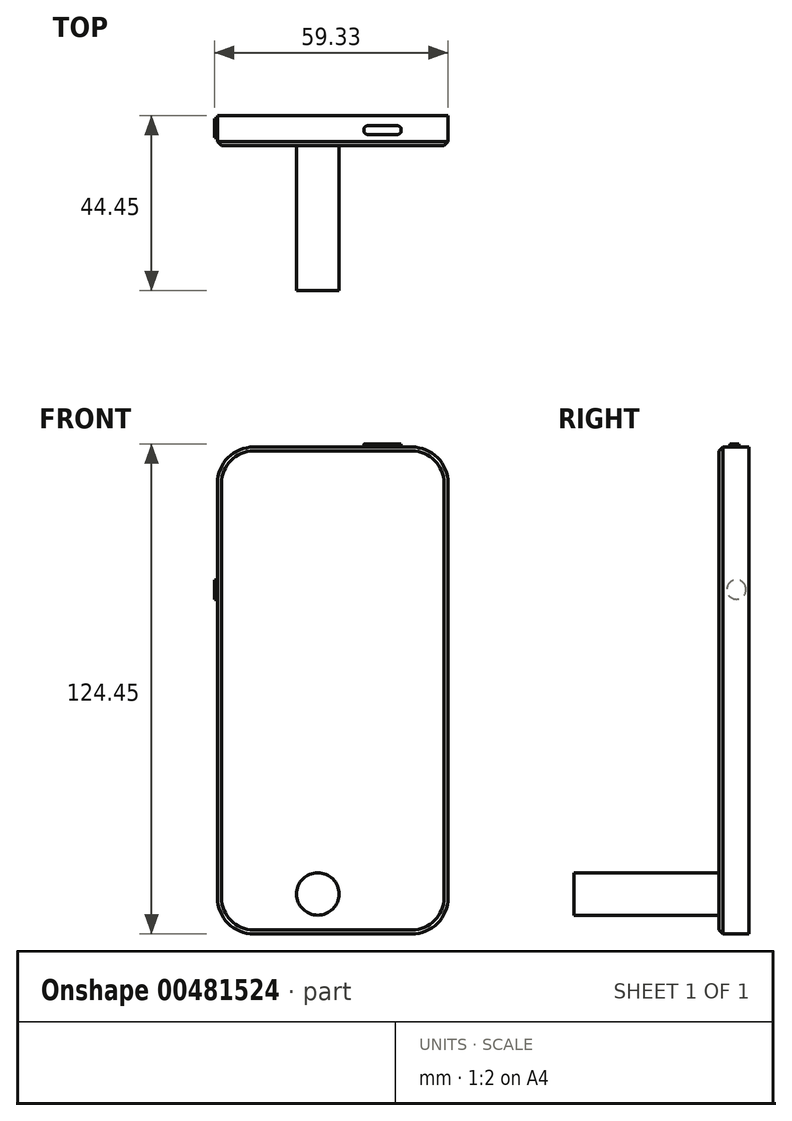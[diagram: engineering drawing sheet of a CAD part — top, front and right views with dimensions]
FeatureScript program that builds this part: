
annotation { "Feature Type Name" : "Feature", "Feature Type Description" : "" }
export const myFeature = defineFeature(function(context is Context, id is Id, definition is map)
    precondition{}
    {
        {
            var Q0;
            Q0=qCreatedBy(makeId("Front.planeOp"),FACE);
            var sketch = newSketch(context, id + "F0", { "sketchPlane" : qUnion([Q0])});
            skLineSegment(sketch, "E0.bottom", {"start": v(-62.59, 53.88) * mm, "end": v(-4.02, 53.88) * mm});
            skLineSegment(sketch, "E0.top", {"start": v(-62.59, -69.81) * mm, "end": v(-4.02, -69.81) * mm});
            skLineSegment(sketch, "E0.left", {"start": v(-62.59, 53.88) * mm, "end": v(-62.59, -69.81) * mm});
            skLineSegment(sketch, "E0.right", {"start": v(-4.02, 53.88) * mm, "end": v(-4.02, -69.81) * mm});
            skSolve(sketch);
        }
        {
            var Q0;
            Q0 = qSketchRegion(id + "F0", true);
            extrude(context, id + "F1", {"entities" : qUnion([Q0]), "depth" : 7.62 * mm});
        }
        {
            var Q0;
            Q0=makeQuery(id+"F1.opExtrude","SWEPT_EDGE",EDGE,{"disambiguationData":[OSD([sQuery(id+"F0.wireOp",EDGE,"E0.top"),sQuery(id+"F0.wireOp",EDGE,"E0.left")])]});
            var Q1;
            Q1=makeQuery(id+"F1.opExtrude","SWEPT_EDGE",EDGE,{"disambiguationData":[OSD([sQuery(id+"F0.wireOp",EDGE,"E0.top"),sQuery(id+"F0.wireOp",EDGE,"E0.right")])]});
            var Q2;
            Q2=makeQuery(id+"F1.opExtrude","SWEPT_EDGE",EDGE,{"disambiguationData":[OSD([sQuery(id+"F0.wireOp",EDGE,"E0.bottom"),sQuery(id+"F0.wireOp",EDGE,"E0.right")])]});
            var Q3;
            Q3=makeQuery(id+"F1.opExtrude","SWEPT_EDGE",EDGE,{"disambiguationData":[OSD([sQuery(id+"F0.wireOp",EDGE,"E0.bottom"),sQuery(id+"F0.wireOp",EDGE,"E0.left")])]});
            fillet(context, id + "F2", {"entities" : qUnion([Q0, Q1, Q2, Q3]), "radius" : 9.16 * mm, "tangentPropagation" : true, "allowEdgeOverflow" : false});
        }
        {
            var Q0;
            Q0=makeQuery(id+"F1.opExtrude","CAP_EDGE",EDGE,{"disambiguationData":[OSD([sQuery(id+"F0.wireOp",EDGE,"E0.bottom")])],"isStart":false});
            chamfer(context, id + "F3", {"entities" : qUnion([Q0]), "width" : 1.02 * mm, "tangentPropagation" : true});
        }
        {
            var Q0;
            Q0=qCreatedBy(makeId("Top.planeOp"),FACE);
            var sketch = newSketch(context, id + "F4", { "sketchPlane" : qUnion([Q0])});
            skLineSegment(sketch, "E1.bottom", {"start": v(-59.32, -32.86) * mm, "end": v(-49.82, -32.86) * mm});
            skLineSegment(sketch, "E1.top", {"start": v(-59.32, -35.06) * mm, "end": v(-49.82, -35.06) * mm});
            skLineSegment(sketch, "E1.left", {"start": v(-59.32, -32.86) * mm, "end": v(-59.32, -35.06) * mm});
            skLineSegment(sketch, "E1.right", {"start": v(-49.82, -32.86) * mm, "end": v(-49.82, -35.06) * mm});
            skSolve(sketch);
        }
        {
            var Q0;
            Q0=makeQuery(id+"F4.imprint","IMPRINT",FACE,{"disambiguationData":[TD([[makeQuery(id+"F4.imprint","IMPRINT",EDGE,{"derivedFrom":sQuery(id+"F4.wireOp",EDGE,"E1.bottom")}),-1.0]])]});
            extrude(context, id + "F5", {"entities" : qUnion([Q0]), "depth" : 0.76 * mm});
        }
        {
            var Q0;
            Q0=makeQuery(id+"F5.opExtrude","SWEPT_BODY",BODY,{"disambiguationData":[OSD([sQuery(id+"F4.wireOp",EDGE,"E1.bottom"),sQuery(id+"F4.wireOp",EDGE,"E1.top"),sQuery(id+"F4.wireOp",EDGE,"E1.left"),sQuery(id+"F4.wireOp",EDGE,"E1.right")])]});
            transform(context, id + "F6", {"entities" : qUnion([Q0]), "transformType" : TransformType.TRANSLATION_3D, "dx" : 27.3 * mm, "dy" : 23.14 * mm, "dz" : 53.87 * mm, "makeCopy" : false});
        }
        {
            var Q0;
            Q0=makeQuery(id+"F5.opExtrude","SWEPT_BODY",BODY,{"disambiguationData":[OSD([sQuery(id+"F4.wireOp",EDGE,"E1.bottom"),sQuery(id+"F4.wireOp",EDGE,"E1.top"),sQuery(id+"F4.wireOp",EDGE,"E1.left"),sQuery(id+"F4.wireOp",EDGE,"E1.right")])]});
            transform(context, id + "F7", {"entities" : qUnion([Q0]), "transformType" : TransformType.TRANSLATION_3D, "dx" : 6.6 * mm, "dy" : 4.06 * mm, "dz" : 0 * mm, "makeCopy" : false});
        }
        {
            var Q0;
            Q0=makeQuery(id+"F5.opExtrude","SWEPT_EDGE",EDGE,{"disambiguationData":[OSD([sQuery(id+"F4.wireOp",EDGE,"E1.top"),sQuery(id+"F4.wireOp",EDGE,"E1.left")])]});
            fillet(context, id + "F8", {"entities" : qUnion([Q0]), "radius" : 0.97 * mm, "tangentPropagation" : true, "allowEdgeOverflow" : false});
        }
        {
            var Q0;
            Q0=makeQuery(id+"F5.opExtrude","SWEPT_EDGE",EDGE,{"disambiguationData":[OSD([sQuery(id+"F4.wireOp",EDGE,"E1.bottom"),sQuery(id+"F4.wireOp",EDGE,"E1.left")])]});
            fillet(context, id + "F9", {"entities" : qUnion([Q0]), "radius" : 0.97 * mm, "tangentPropagation" : true, "allowEdgeOverflow" : false});
        }
        {
            var Q0;
            Q0=makeQuery(id+"F5.opExtrude","SWEPT_EDGE",EDGE,{"disambiguationData":[OSD([sQuery(id+"F4.wireOp",EDGE,"E1.top"),sQuery(id+"F4.wireOp",EDGE,"E1.right")])]});
            fillet(context, id + "F10", {"entities" : qUnion([Q0]), "radius" : 0.97 * mm, "tangentPropagation" : true, "allowEdgeOverflow" : false});
        }
        {
            var Q0;
            Q0=makeQuery(id+"F5.opExtrude","SWEPT_EDGE",EDGE,{"disambiguationData":[OSD([sQuery(id+"F4.wireOp",EDGE,"E1.bottom"),sQuery(id+"F4.wireOp",EDGE,"E1.right")])]});
            fillet(context, id + "F11", {"entities" : qUnion([Q0]), "radius" : 0.98 * mm, "tangentPropagation" : true, "allowEdgeOverflow" : false});
        }
        {
            var Q0;
            Q0=makeQuery(id+"F5.opExtrude","SWEPT_BODY",BODY,{"disambiguationData":[OSD([sQuery(id+"F4.wireOp",EDGE,"E1.bottom"),sQuery(id+"F4.wireOp",EDGE,"E1.top"),sQuery(id+"F4.wireOp",EDGE,"E1.left"),sQuery(id+"F4.wireOp",EDGE,"E1.right")])]});
            transform(context, id + "F12", {"entities" : qUnion([Q0]), "transformType" : TransformType.TRANSLATION_3D, "dx" : 0 * mm, "dy" : 3.07 * mm, "dz" : 0 * mm, "makeCopy" : false});
        }
        {
            var Q0;
            Q0=qCreatedBy(makeId("Right.planeOp"),FACE);
            var sketch = newSketch(context, id + "F13", { "sketchPlane" : qUnion([Q0])});
            skCircle(sketch, "E2", {"center": v(-24.5, 17.66) * mm, "radius": 2.45 * mm});
            skSolve(sketch);
        }
        {
            var Q0;
            Q0=makeQuery(id+"F13.imprint","IMPRINT",FACE,{"disambiguationData":[TD([[makeQuery(id+"F13.imprint","IMPRINT",EDGE,{"derivedFrom":sQuery(id+"F13.wireOp",EDGE,"E2")}),1.0]])]});
            extrude(context, id + "F14", {"entities" : qUnion([Q0]), "operationType" : NewBodyOperationType.ADD, "depth" : 0.76 * mm});
        }
        {
            var Q0;
            Q0=makeQuery(id+"F14.opExtrude","SWEPT_BODY",BODY,{"disambiguationData":[OSD([sQuery(id+"F13.wireOp",EDGE,"E2")])]});
            transform(context, id + "F15", {"entities" : qUnion([Q0]), "transformType" : TransformType.TRANSLATION_3D, "dx" : -63.75 * mm, "dy" : 0 * mm, "dz" : 0 * mm, "makeCopy" : false});
        }
        {
            var Q0;
            Q0=makeQuery(id+"F14.opExtrude","SWEPT_BODY",BODY,{"disambiguationData":[OSD([sQuery(id+"F13.wireOp",EDGE,"E2")])]});
            transform(context, id + "F16", {"entities" : qUnion([Q0]), "transformType" : TransformType.TRANSLATION_3D, "dx" : 0 * mm, "dy" : 21.34 * mm, "dz" : 0 * mm, "makeCopy" : false});
        }
        {
            var Q0;
            Q0=makeQuery(id+"F14.opExtrude","SWEPT_BODY",BODY,{"disambiguationData":[OSD([sQuery(id+"F13.wireOp",EDGE,"E2")])]});
            transform(context, id + "F17", {"entities" : qUnion([Q0]), "transformType" : TransformType.TRANSLATION_3D, "dx" : 0.4 * mm, "dy" : 0 * mm, "dz" : 0 * mm, "makeCopy" : false});
        }
        {
            var Q0;
            Q0=qCreatedBy(makeId("Front.planeOp"),FACE);
            var sketch = newSketch(context, id + "F18", { "sketchPlane" : qUnion([Q0])});
            skCircle(sketch, "E3", {"center": v(-37.1, -59.67) * mm, "radius": 5.39 * mm});
            skSolve(sketch);
        }
        {
            var Q0;
            Q0=makeQuery(id+"F18.imprint","IMPRINT",FACE,{"disambiguationData":[TD([[makeQuery(id+"F18.imprint","IMPRINT",EDGE,{"derivedFrom":sQuery(id+"F18.wireOp",EDGE,"E3")}),1.0]])]});
            extrude(context, id + "F19", {"entities" : qUnion([Q0]), "operationType" : NewBodyOperationType.ADD, "depth" : 44.45 * mm});
        }
    });
